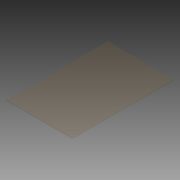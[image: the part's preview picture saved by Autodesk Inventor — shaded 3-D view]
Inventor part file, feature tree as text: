
AUTODESK INVENTOR PART (.ipt)
format: ipt  version: 2012 (Build 160160000, 160)  size: 65,536 bytes
history: native  units: in
note: dims shown in document units (in); Inventor stores cm internally (conversion verified against a paired STEP export)
features: extrude x1, sketch x1
ambient origin geometry x8: Origin, YZ Plane, XZ Plane, XY Plane, X Axis, Y Axis, Z Axis, Center Point
bodies: Solid1 (feature_tree)
feature tree (2):
  extrude  "Extrusion1"  Depth=11.25in
  sketch  "Sketch1"  dims[d0=0.125in d1=11.25in d2=17.25in d3=0.0in]
